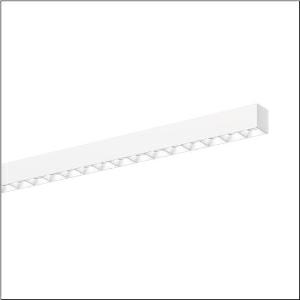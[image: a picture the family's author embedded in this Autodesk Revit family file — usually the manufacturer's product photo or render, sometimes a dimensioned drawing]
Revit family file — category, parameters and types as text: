
# Revit family: silica_r__21_51mx26da34wb_607f
name_source: partatom
category: Lighting Fixtures
units: mm (PartAtom-declared; Revit-internal decimal feet)

## family parameters
Cut with Voids When Loaded = No
Host = Face
Light Source = No
Part Type = Normal
Room Calculation Point = No
Round Connector Dimension = Use Diameter
Shared = No

## types (1)
- --- (1 x LED, 4320 lm, 25.1 W, 3000K)
    Apparent Load = 25 VA
    CIE Flux Codes = 83 98 100 100 100
    Color Rendering = 80
    Color Temperature = 3000K
    Default Elevation = 1800 mm
    Description = Silica® 21, office luminaire, primary light control with darklight reflector, of PMMA, white, CAT 2 (L<= 3000cd/m²), light emission: direct distribution, primary light characteristic: symmetric, installation type: surface-mounted, LED, rated luminous flux: 4.320lm, luminous efficacy: 172lm/W, light colour: 830, colour temperature: 3000K, with terminal, 3+2-pole, max. 2.5mm², mains connection: 220..240V, AC, 50/60Hz, rated input power: 25.1W, luminaire housing, of aluminium, traffic white (RAL 9016), length: 1.204mm, width: 53mm, height: 53mm, protection rating (complete): IP20, insulation class (complete): insulation class I (protective earthing), certification: CE, permissible operating ambient temperature: 0..+35°C, standard: EN 50419, packaging unit: 1 piece
    Height = 0 mm  [stored 0 ft]
    Lamp = 1 x LED
    Lamp Light Flux = 4320 lm
    Lamp Power = 25.1 W
    Lamp count = 1
    Length = 1204 mm
    Luminous efficacy = 172 lm/W
    Manufacturer = Siteco
    ModVariant = No
    Model = 51MX26DA34WB
    Mounting Place = Ceiling
    Mounting Type = Recessed
    Number of Poles = 1
    OnlyDefault = Yes
    Power Factor = 1
    Product Name = Silica® 21
    Product group = office luminaire | ceiling recessed
    ProductGroupID = 401
    Protection Class = Protection class I
    Protection Degree = IP 20
    RLX_Detail_Level = 1
    RLX_Emergency_Light_Flux = 0 lm
    RLX_Emergency_Type = 0
    RLX_Emergency_Type_DB = No
    RlxData = <blob elided: 38257 chars, md5=b090fd38>
    Socket = socket
    Standby Power = 0 W
    System Light Flux = 4320 lm
    System Power = 25 W
    Type Comments = factory setting: luminous flux: 100 % | dim-lin: 254 | 360 mA
    Type Image = l_1313597.jpg
    URL = http://relux.com
    VarID = @adj_073609
    Voltage = 0 V
    Weight = 0.00 kg
    Width = 53 mm

note: [stored X ft] marks values corroborated as IEEE doubles in the binary element streams (Revit-internal decimal feet)

## geometry (parser evidence)
native form markers: Blend x4, Sweep x10
no freeform markers — native parametric forms only
